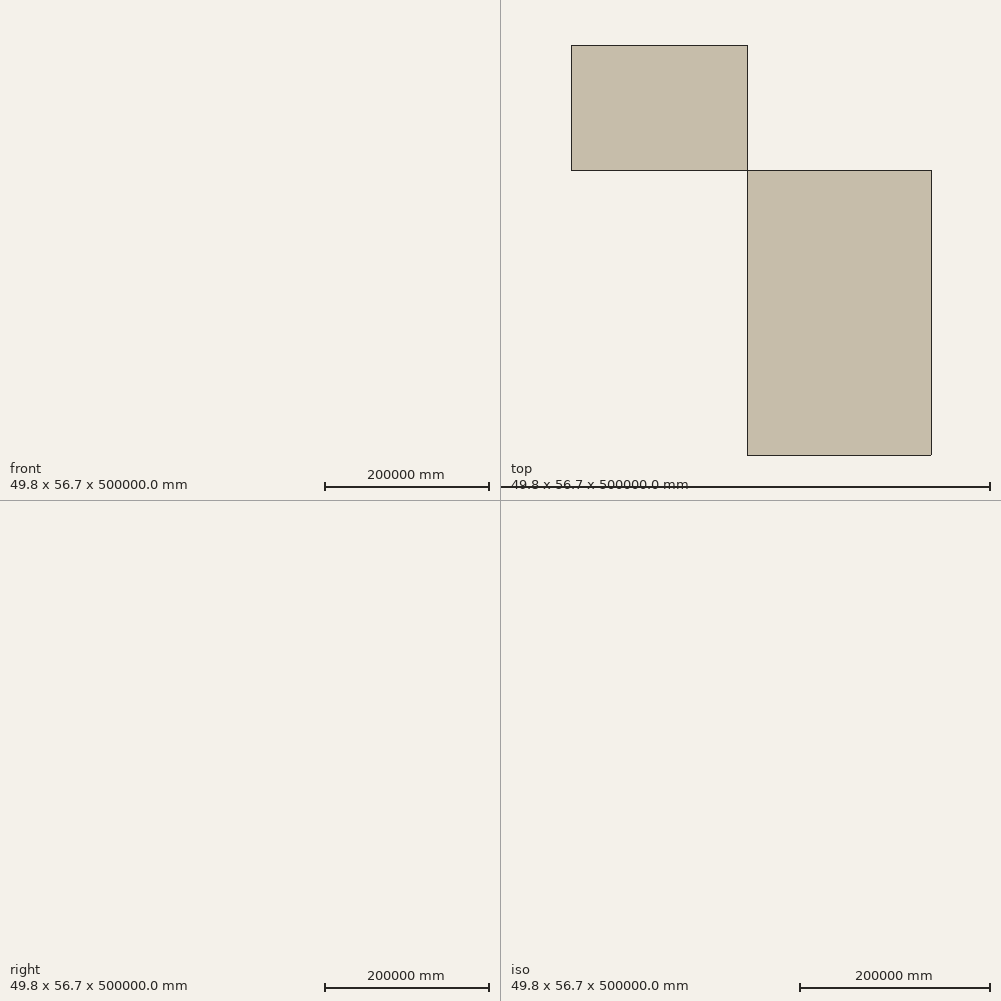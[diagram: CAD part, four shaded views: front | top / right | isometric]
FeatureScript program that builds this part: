
annotation { "Feature Type Name" : "Feature", "Feature Type Description" : "" }
export const myFeature = defineFeature(function(context is Context, id is Id, definition is map)
    precondition{}
    {
        {
            var Q0;
            Q0=qCreatedBy(makeId("Top.planeOp"),FACE);
            var sketch = newSketch(context, id + "F0", { "sketchPlane" : qUnion([Q0])});
            skLineSegment(sketch, "E0.bottom", {"start": v(0, 0) * mm, "end": v(-24.38, 0) * mm});
            skLineSegment(sketch, "E0.top", {"start": v(0, 17.32) * mm, "end": v(-24.38, 17.32) * mm});
            skLineSegment(sketch, "E0.left", {"start": v(0, 0) * mm, "end": v(0, 17.32) * mm});
            skLineSegment(sketch, "E0.right", {"start": v(-24.38, 0) * mm, "end": v(-24.38, 17.32) * mm});
            skSolve(sketch);
        }
        {
            var Q0;
            Q0 = qSketchRegion(id + "F0", true);
            extrude(context, id + "F1", {"entities" : qUnion([Q0]), "depth" : 500000 * mm});
        }
        {
            var Q0;
            Q0=qCreatedBy(makeId("Right.planeOp"),FACE);
            var sketch = newSketch(context, id + "F2", { "sketchPlane" : qUnion([Q0])});
            skLineSegment(sketch, "E1.bottom", {"start": v(0, 0) * mm, "end": v(-39.35, 0) * mm});
            skLineSegment(sketch, "E1.top", {"start": v(0, 21.62) * mm, "end": v(-39.35, 21.62) * mm});
            skLineSegment(sketch, "E1.left", {"start": v(0, 0) * mm, "end": v(0, 21.62) * mm});
            skLineSegment(sketch, "E1.right", {"start": v(-39.35, 0) * mm, "end": v(-39.35, 21.62) * mm});
            skSolve(sketch);
        }
        {
            var Q0;
            Q0=makeQuery(id+"F2.imprint","IMPRINT",FACE,{"disambiguationData":[TD([[makeQuery(id+"F2.imprint","IMPRINT",EDGE,{"derivedFrom":sQuery(id+"F2.wireOp",EDGE,"E1.bottom")}),-1.0]])]});
            extrude(context, id + "F3", {"entities" : qUnion([Q0]), "depth" : 25.4 * mm});
        }
    });
